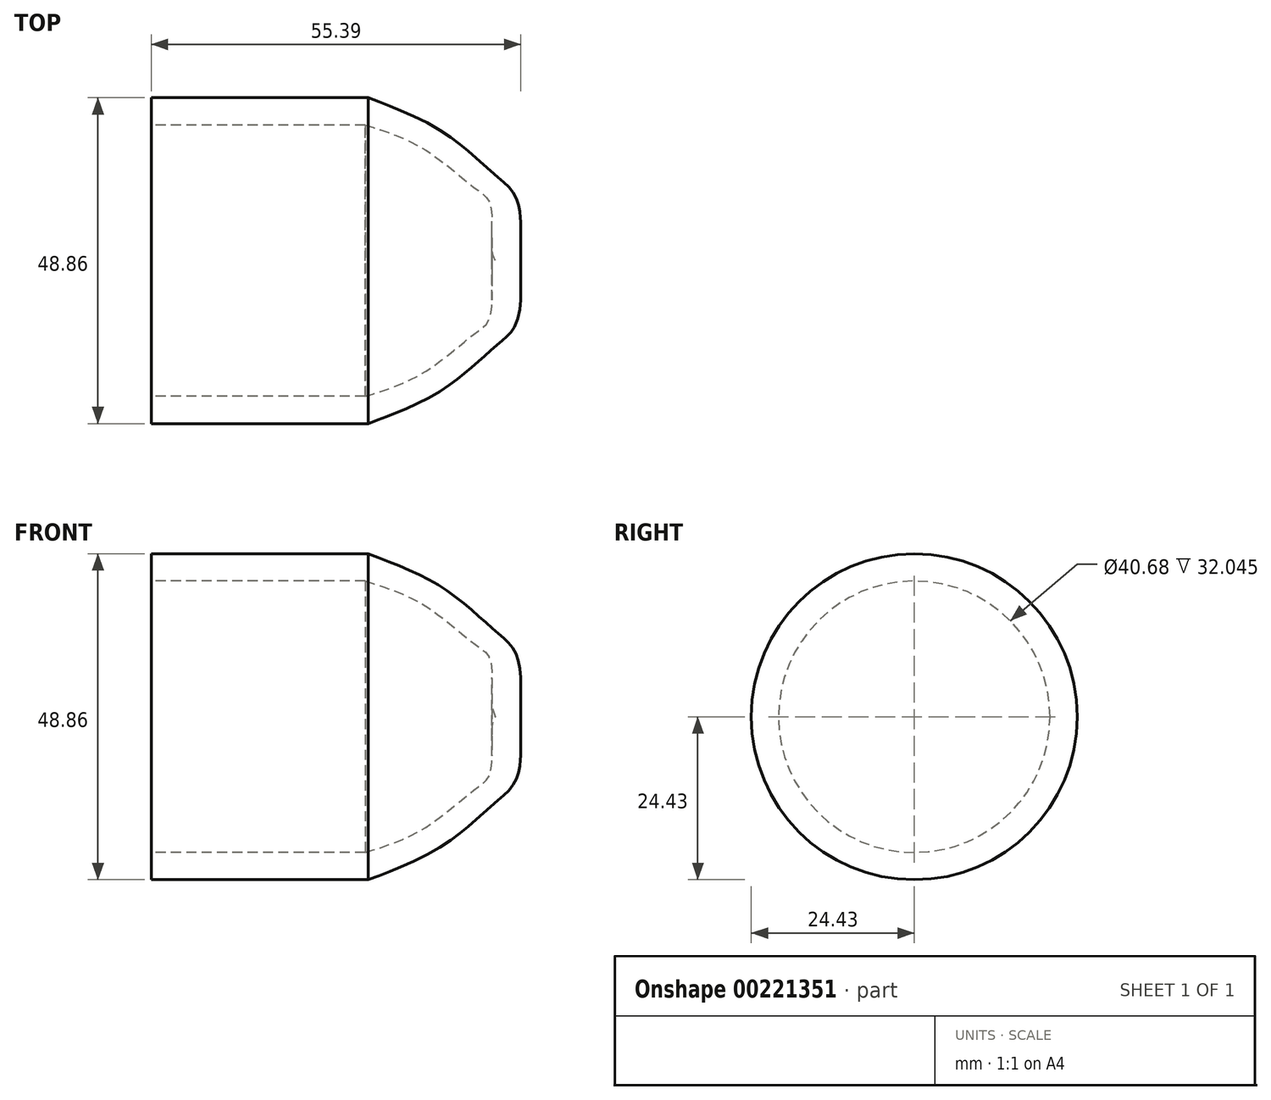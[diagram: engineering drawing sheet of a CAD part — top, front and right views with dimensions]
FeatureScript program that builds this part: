
annotation { "Feature Type Name" : "Feature", "Feature Type Description" : "" }
export const myFeature = defineFeature(function(context is Context, id is Id, definition is map)
    precondition{}
    {
        {
            var Q0;
            Q0=qCreatedBy(makeId("Front.planeOp"),FACE);
            var sketch = newSketch(context, id + "F0", { "sketchPlane" : qUnion([Q0])});
            skLineSegment(sketch, "E0", {"start": v(0, 24.43) * mm, "end": v(32.5, 24.43) * mm});
            skFitSpline(sketch, "E1", {"points": [v(32.5, 24.43) * mm, v(43.86, 19.2) * mm, v(51.6, 12.84) * mm, v(54.77, 9.2) * mm, v(55.23, 0) * mm], "startDerivative": vector(40.2, -15.15) * mm, "endDerivative": vector(-2.27, -41.57) * mm});
            skLineSegment(sketch, "E2", {"start": v(-47.73, 0) * mm, "end": v(70.9, 0) * mm});
            skLineSegment(sketch, "E3", {"start": v(0, 24.43) * mm, "end": v(0, 20.34) * mm});
            skLineSegment(sketch, "E4", {"start": v(0, 20.34) * mm, "end": v(32.05, 20.34) * mm});
            skFitSpline(sketch, "E5", {"points": [v(32.05, 20.34) * mm, v(40.9, 16.7) * mm, v(48.64, 10.8) * mm, v(50.9, 8.07) * mm, v(51.6, 0) * mm, v(55.23, 0) * mm], "startDerivative": vector(37.07, -11.53) * mm, "endDerivative": vector(29.9, 9.42) * mm});
            skSolve(sketch);
        }
        {
            var Q0;
            Q0=makeQuery(id+"F0.imprint","IMPRINT",FACE,{"disambiguationData":[TD([[makeQuery(id+"F0.imprint","IMPRINT",EDGE,{"derivedFrom":sQuery(id+"F0.wireOp",EDGE,"E0")}),-1.0]])]});
            var Q1;
            Q1=sQuery(id+"F0.wireOp",EDGE,"E2");
            revolve(context, id + "F1", {"entities" : qUnion([Q0]), "axis" : qUnion([Q1]), "revolveType" : RevolveType.FULL});
        }
    });
